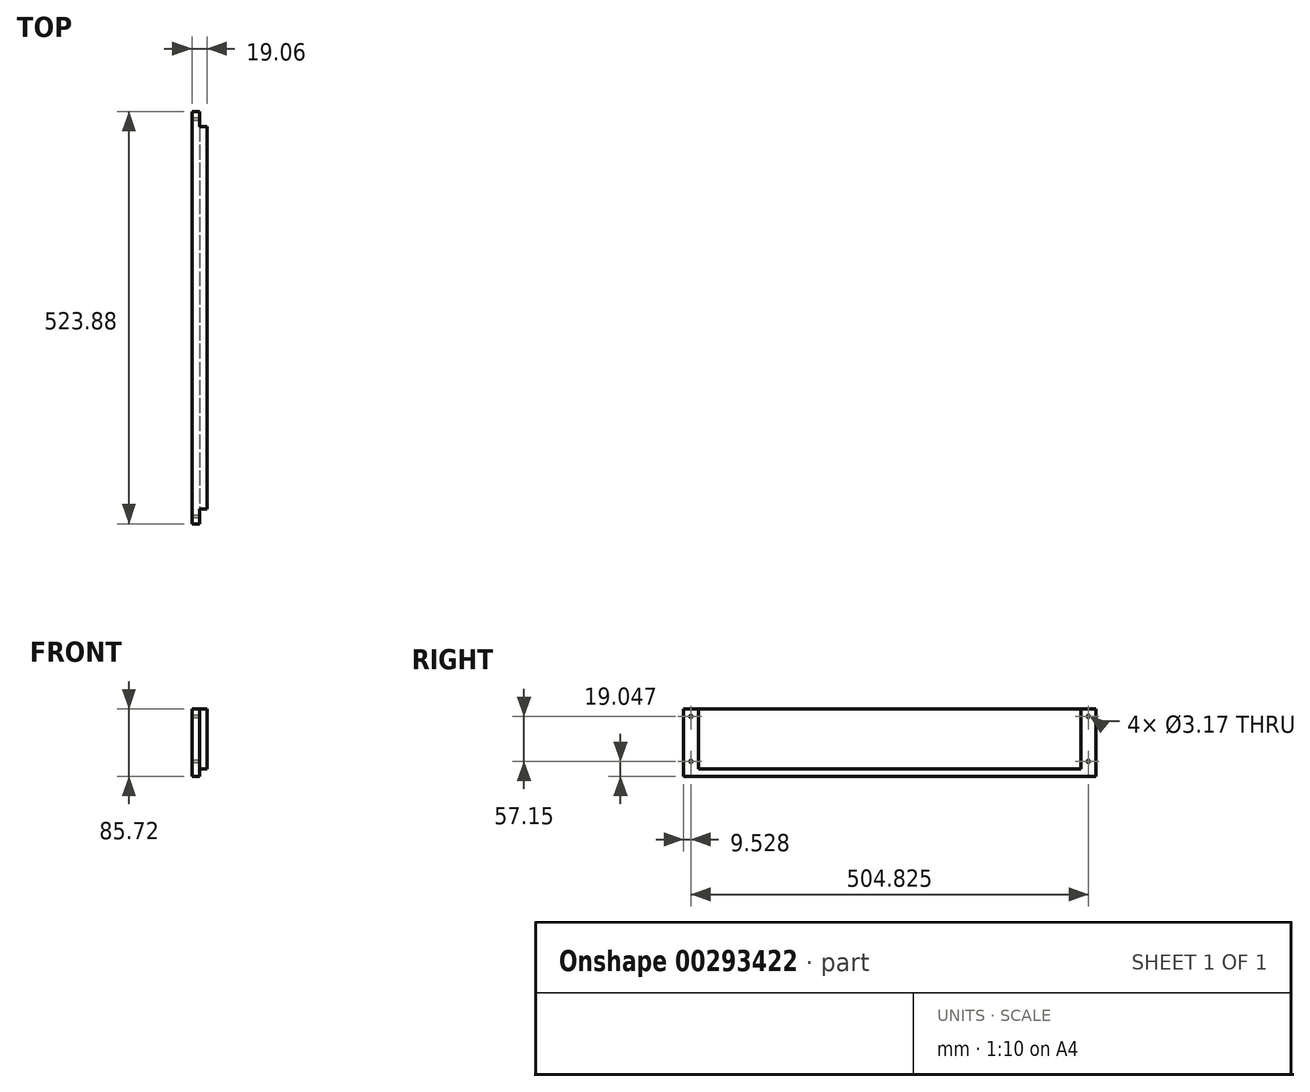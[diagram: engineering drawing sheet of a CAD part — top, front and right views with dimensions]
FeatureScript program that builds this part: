
annotation { "Feature Type Name" : "Feature", "Feature Type Description" : "" }
export const myFeature = defineFeature(function(context is Context, id is Id, definition is map)
    precondition{}
    {
        {
            var Q0;
            Q0=qCreatedBy(makeId("Right.planeOp"),FACE);
            var sketch = newSketch(context, id + "F0", { "sketchPlane" : qUnion([Q0])});
            skLineSegment(sketch, "E0.bottom", {"start": v(261.94, -42.86) * mm, "end": v(-261.94, -42.86) * mm});
            skLineSegment(sketch, "E0.top", {"start": v(261.94, 42.86) * mm, "end": v(-261.94, 42.86) * mm});
            skLineSegment(sketch, "E0.left", {"start": v(261.94, -42.86) * mm, "end": v(261.94, 42.86) * mm});
            skLineSegment(sketch, "E0.right", {"start": v(-261.94, -42.86) * mm, "end": v(-261.94, 42.86) * mm});
            skPoint(sketch, "E0.middle", {"position": v(0, 0) * mm});
            skLineSegment(sketch, "E1.bottom", {"start": v(242.89, -33.34) * mm, "end": v(-242.89, -33.34) * mm});
            skLineSegment(sketch, "E2", {"start": v(-242.89, -33.34) * mm, "end": v(-242.89, 42.86) * mm});
            skLineSegment(sketch, "E3", {"start": v(242.89, -33.34) * mm, "end": v(242.89, 42.86) * mm});
            skCircle(sketch, "E4", {"center": v(-252.41, 33.34) * mm, "radius": 1.59 * mm});
            skCircle(sketch, "E5", {"center": v(-252.41, -23.81) * mm, "radius": 1.59 * mm});
            skCircle(sketch, "E6.MirrorC", {"center": v(252.41, 33.34) * mm, "radius": 1.59 * mm});
            skCircle(sketch, "E7.MirrorC", {"center": v(252.41, -23.81) * mm, "radius": 1.59 * mm});
            skSolve(sketch);
        }
        {
            var Q0;
            Q0=makeQuery(id+"F0.imprint","IMPRINT",FACE,{"disambiguationData":[TD([[makeQuery(id+"F0.imprint","IMPRINT",EDGE,{"derivedFrom":sQuery(id+"F0.wireOp",EDGE,"E1.bottom")}),-1.0]])]});
            extrude(context, id + "F1", {"entities" : qUnion([Q0]), "depth" : 9.52 * mm});
        }
        {
            var Q0;
            Q0=makeQuery(id+"F0.imprint","IMPRINT",FACE,{"disambiguationData":[TD([[makeQuery(id+"F0.imprint","IMPRINT",EDGE,{"derivedFrom":sQuery(id+"F0.wireOp",EDGE,"E0.bottom")}),-1.0]])]});
            var Q1;
            Q1=makeQuery(id+"F0.imprint","IMPRINT",FACE,{"disambiguationData":[TD([[makeQuery(id+"F0.imprint","IMPRINT",EDGE,{"derivedFrom":sQuery(id+"F0.wireOp",EDGE,"E1.bottom")}),-1.0]])]});
            extrude(context, id + "F2", {"entities" : qUnion([Q0, Q1]), "operationType" : NewBodyOperationType.ADD, "oppositeDirection" : true, "depth" : 9.52 * mm});
        }
    });
